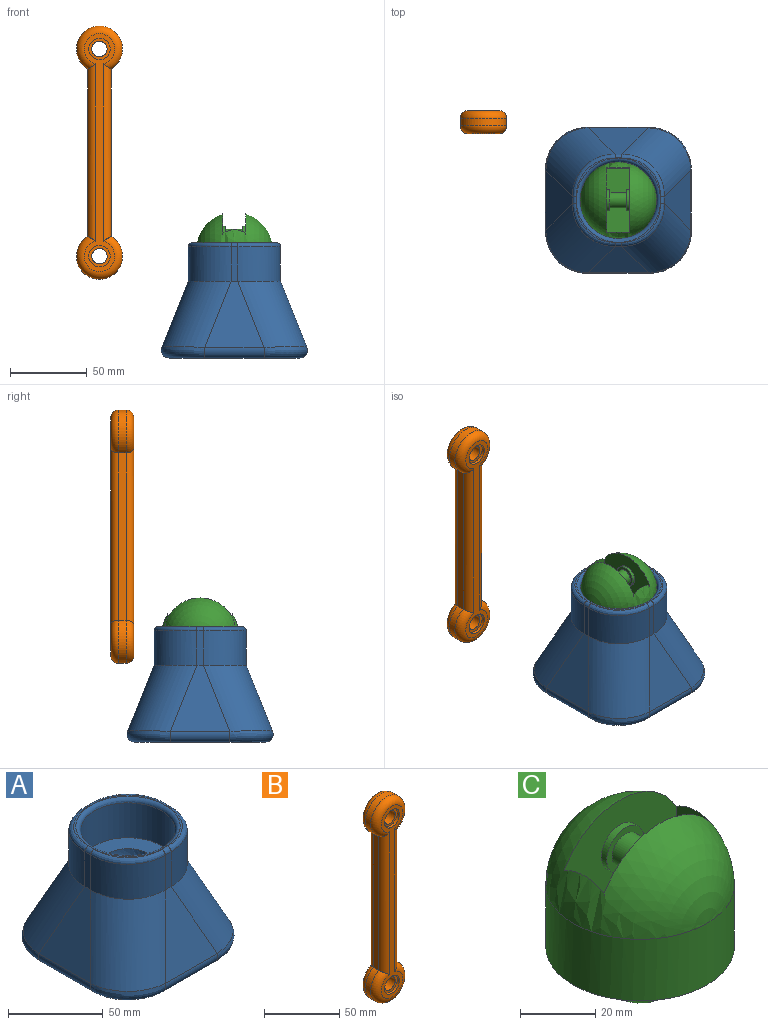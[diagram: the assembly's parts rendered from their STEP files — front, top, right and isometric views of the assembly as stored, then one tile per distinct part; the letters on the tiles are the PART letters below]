
ASSEMBLY  parts=3 mates=1
PART A: 41 faces, bbox 100.2x100.2x75 mm
  f0: plane 27.5x27.5mm, normal (0,0,1), area 30.8mm2, adj f32,f33,f34,f35
  f1: plane 27.5x27.5mm, normal (0,0,1), area 30.8mm2, adj f32,f34,f36,f38
  f2: plane 27.5x27.5mm, normal (0,0,1), area 30.8mm2, adj f32,f38,f39,f40
  f3: plane 85.23x85.23mm, normal (0,0,-1), area 6821.3mm2, adj f8,f9,f10,f11,f13,f15,f17,f19
  f4: plane 43.14x38.81mm, normal (0,-0.93,0.37), area 1001.3mm2, adj f10,f14,f18,f21
  f5: plane 43.14x38.81mm, normal (0.93,0,0.37), area 1001.3mm2, adj f8,f16,f18,f23
  f6: plane 43.14x38.81mm, normal (0,0.93,0.37), area 1001.3mm2, adj f9,f12,f16,f25
  f7: plane 43.14x38.81mm, normal (-0.93,0,0.37), area 1001.3mm2, adj f11,f12,f14,f28
  f8: cylinder r=5mm len=38.81mm, axis (0,-1,0), area 378.6mm2, adj f3,f5,f17,f19
  f9: cylinder r=5mm len=38.81mm, axis (-1,0,0), area 378.6mm2, adj f3,f6,f13,f17
  f10: cylinder r=5mm len=38.81mm, axis (-1,0,0), area 378.6mm2, adj f3,f4,f15,f19
  f11: cylinder r=5mm len=38.81mm, axis (0,-1,0), area 378.6mm2, adj f3,f7,f13,f15
  f12: cylinder r=30mm len=49.81mm, axis (0.35,-0.35,0.87), area 2110.3mm2, adj f6,f7,f13,f26
  f13: bspline ~34.54x34.54mm, area 430.9mm2, adj f3,f9,f11,f12
  f14: cylinder r=30mm len=49.81mm, axis (-0.35,-0.35,-0.87), area 2110.3mm2, adj f4,f7,f15,f20
  f15: bspline ~28.22x28.22mm, area 430.9mm2, adj f3,f10,f11,f14
  f16: cylinder r=30mm len=49.81mm, axis (0.35,0.35,-0.87), area 2110.3mm2, adj f5,f6,f17,f24
  f17: bspline ~28.22x28.22mm, area 430.9mm2, adj f3,f8,f9,f16
  f18: cylinder r=30mm len=49.81mm, axis (-0.35,0.35,0.87), area 2110.3mm2, adj f4,f5,f19,f22
  f19: bspline ~34.54x34.54mm, area 430.9mm2, adj f3,f8,f10,f18
  f20: extruded ~27.85x27.85mm, area 990.3mm2, adj f14,f21,f28,f37
  f21: plane 22.5x4.29mm, normal (0,-1,0), area 96.6mm2, adj f4,f20,f22,f35
  f22: extruded ~27.85x27.85mm, area 990.3mm2, adj f18,f21,f23,f33
  f23: plane 22.5x4.29mm, normal (1,0,0), area 96.6mm2, adj f5,f22,f24,f34
  f24: extruded ~27.85x27.85mm, area 990.3mm2, adj f16,f23,f25,f36
  f25: plane 22.5x4.29mm, normal (0,1,0), area 96.6mm2, adj f6,f24,f26,f38
  f26: extruded ~27.85x27.85mm, area 990.3mm2, adj f12,f25,f28,f40
  f27: cylinder r=25mm len=50mm, axis (0,0,-1), area 3534.3mm2, adj f31,f32
  f28: plane 22.5x4.29mm, normal (-1,0,0), area 96.6mm2, adj f7,f20,f26,f39
  f29: plane 27.5x27.5mm, normal (0,0,1), area 30.8mm2, adj f32,f35,f37,f39
  f30: sphere r=15mm, area 1413.7mm2, adj f31
  f31: plane 50x50mm, normal (0,0,1), area 1256.6mm2, adj f27,f30
  f32: torus R=27.5mm, axis (0,0,1), area 639.3mm2, adj f0,f1,f2,f27,f29
  f33: bspline ~32.23x32.23mm, area 167.2mm2, adj f0,f22,f34,f35
  f34: cylinder r=2.5mm len=4.29mm, axis (0,-1,0), area 16.9mm2, adj f0,f1,f23,f33,f36
  f35: cylinder r=2.5mm len=4.29mm, axis (-1,0,0), area 16.9mm2, adj f0,f21,f29,f33,f37
  f36: bspline ~32.23x32.23mm, area 167.2mm2, adj f1,f24,f34,f38
  f37: bspline ~32.23x32.23mm, area 167.2mm2, adj f20,f29,f35,f39
  f38: cylinder r=2.5mm len=4.29mm, axis (1,0,0), area 16.9mm2, adj f1,f2,f25,f36,f40
  f39: cylinder r=2.5mm len=4.29mm, axis (0,1,0), area 16.9mm2, adj f2,f28,f29,f37,f40
  f40: bspline ~32.23x32.23mm, area 167.2mm2, adj f2,f26,f38,f39
PART B: 24 faces, bbox 32.5x15x167.5 mm
  f0: cylinder r=5mm len=11mm, axis (0,-1,0), area 345.6mm2, adj f19,f22
  f1: cylinder r=5mm len=11mm, axis (0,-1,0), area 345.6mm2, adj f17,f20
  f2: plane 109.02x5mm, normal (1,0,0), area 545.1mm2, adj f3,f5,f8,f12
  f3: cylinder r=15mm len=30mm, axis (0,1,0), area 392.7mm2, adj f2,f4,f9,f13
  f4: plane 109.02x5mm, normal (-1,0,0), area 545.1mm2, adj f3,f5,f11,f15
  f5: cylinder r=15mm len=30mm, axis (0,1,0), area 392.7mm2, adj f2,f4,f10,f14
  f6: plane 155x20mm, normal (0,-1,0), area 896.5mm2, adj f12,f13,f14,f15,f16,f18
  f7: plane 155x20mm, normal (0,1,0), area 896.5mm2, adj f8,f9,f10,f11,f21,f23
  f8: cylinder r=5mm len=115.64mm, axis (0,0,1), area 874.1mm2, adj f2,f7,f9,f10
  f9: torus R=10mm, axis (0,-1,0), area 558mm2, adj f3,f7,f8,f11
  f10: torus R=10mm, axis (0,-1,0), area 558mm2, adj f5,f7,f8,f11
  f11: cylinder r=5mm len=115.64mm, axis (0,0,-1), area 874.1mm2, adj f4,f7,f9,f10
  f12: cylinder r=5mm len=115.64mm, axis (0,0,-1), area 874.1mm2, adj f2,f6,f13,f14
  f13: torus R=10mm, axis (0,-1,0), area 558mm2, adj f3,f6,f12,f15
  f14: torus R=10mm, axis (0,-1,0), area 558mm2, adj f5,f6,f12,f15
  f15: cylinder r=5mm len=115.64mm, axis (0,0,1), area 874.1mm2, adj f4,f6,f13,f14
  f16: cylinder r=7mm len=14mm, axis (0,-1,0), area 88mm2, adj f6,f17
  f17: plane 14x14mm, normal (0,-1,0), area 75.4mm2, adj f1,f16
  f18: cylinder r=7mm len=14mm, axis (0,-1,0), area 88mm2, adj f6,f19
  f19: plane 14x14mm, normal (0,-1,0), area 75.4mm2, adj f0,f18
  f20: plane 14x14mm, normal (0,1,0), area 75.4mm2, adj f1,f21
  f21: cylinder r=7mm len=14mm, axis (0,1,0), area 88mm2, adj f7,f20
  f22: plane 14x14mm, normal (0,1,0), area 75.4mm2, adj f0,f23
  f23: cylinder r=7mm len=14mm, axis (0,1,0), area 88mm2, adj f7,f22
PART C: 14 faces, bbox 50x50x60 mm
  f0: sphere r=25mm, area 3160.2mm2, adj f1,f4,f5,f6,f7
  f1: cylinder r=25mm len=50mm, axis (0,0,1), area 3141.6mm2, adj f0,f2
  f2: plane 50x50mm, normal (0,0,-1), area 1256.6mm2, adj f1,f3
  f3: sphere r=15mm, area 1413.7mm2, adj f2
  f4: plane 28.56x15mm, normal (-1,0,0), area 417.6mm2, adj f0,f5,f7,f8
  f5: plane 42x38.85mm, normal (0,1,0), area 1326mm2, adj f0,f4,f6,f8,f9
  f6: plane 28.56x15mm, normal (1,0,0), area 417.6mm2, adj f0,f5,f7,f8
  f7: plane 42x38.85mm, normal (0,-1,0), area 1326mm2, adj f0,f4,f6,f8,f12
  f8: plane 42x15mm, normal (0,0,1), area 630mm2, adj f4,f5,f6,f7
  f9: cylinder r=7mm len=14mm, axis (0,-1,0), area 88mm2, adj f5,f10
  f10: plane 14x14mm, normal (0,1,0), area 75.4mm2, adj f9,f11
  f11: cylinder r=5mm len=11mm, axis (0,-1,0), area 345.6mm2, adj f10,f13
  f12: cylinder r=7mm len=14mm, axis (0,1,0), area 88mm2, adj f7,f13
  f13: plane 14x14mm, normal (0,-1,0), area 75.4mm2, adj f11,f12
PLACE A t=(-9.38,-4.08,-37.5)mm fixed
PLACE B t=(-189.01,104.1,28.49)mm
PLACE C rot(axis=(0,0,1),90deg) t=(89.85,155.07,32.5)mm
MATE revolute C.f1 <-> A.f27  axis (0,0,1) through (40.62,45.92,12.5)mm
